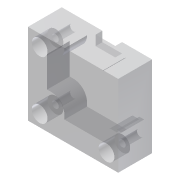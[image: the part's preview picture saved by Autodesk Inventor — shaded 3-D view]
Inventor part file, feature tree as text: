
AUTODESK INVENTOR PART (.ipt)
format: ipt  version: 2015 SP1 (Build 190203100, 203)  size: 254,976 bytes
history: native  units: mm
features: extrude x6, sketch x3, other x1
ambient origin geometry x8: Origin, YZ Plane, XZ Plane, XY Plane, X Axis, Y Axis, Z Axis, Center Point
bodies: Body1 (feature_tree)
feature tree (10):
  other  "Твердое тело1"
  extrude  "Выдавливание1"  Depth=36.0mm
  extrude  "Выдавливание2"  Depth=32.0mm
  extrude  "Выдавливание3"  Depth=3.18mm
  extrude  "Выдавливание5"  Depth=3.18mm
  extrude  "Выдавливание6"  Depth=3.18mm
  extrude  "Выдавливание7"  Depth=3.18mm
  sketch  "Эскиз2"
  sketch  "Эскиз3"
  sketch  "Эскиз4"
